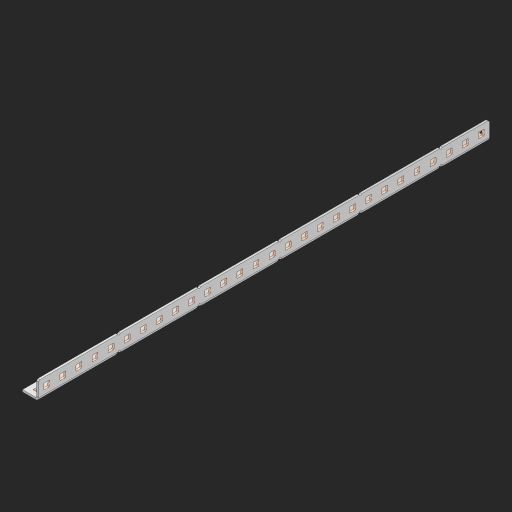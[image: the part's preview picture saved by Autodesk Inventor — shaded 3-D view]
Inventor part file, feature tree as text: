
AUTODESK INVENTOR PART (.ipt)
format: ipt  version: 2023 (Build 270158000, 158)  size: 921,088 bytes
history: native  units: in
note: dims shown in document units (in); Inventor stores cm internally (conversion verified against a paired STEP export)
features: other x61, extrude x55, sheet_metal_op x10, sketch x8, mirror x1, pattern_linear x1, chamfer x1
ambient origin geometry x8: Origin, YZ Plane, XZ Plane, XY Plane, X Axis, Y Axis, Z Axis, Center Point
bodies: Solid1 (feature_tree), Body (feature_tree)
feature tree (137):
  other  "Flange Pattern Plane"
  sheet_metal_op  "Flange Pattern"
  sheet_metal_op  "Body Pattern"
  other  "Arc Length"
  mirror  "Notch Mirror"
  pattern_linear  "Notch Pattern"  Spacing1=0.25in  [1 undecoded]
  chamfer  "End Chamfer"
  extrude  "Half Cut"  Depth=0.0625in
  sketch  "Sketch1"  dims[d0=1.5in]
  other  "Plate1"
  sketch  "Sketch2"  dims[d1=14.0in]
  other  "Plate2"
  sheet_metal_op  "Bend1"
  sheet_metal_op  "Corner1"
  sketch  "Sketch3"  dims[d2=0.0625in]
  other  "Flange Pattern Sketch"
  sketch  "Sketch7"  dims[d3=0.0625in]
  other  "Srf1"
  other  "Srf2"
  sketch  "Sketch8"  dims[d4=0.0312in]
  sketch  "Sketch9"  dims[d5=0.125in]
  other  "Srf91"
  sheet_metal_op  "Body Pattern Sketch"
  other  "Srf92"
  sketch  "Sketch13"  dims[d6=0.0625in]
  sketch  "Sketch14"  dims[d7=0.5in d8=90.0deg d9=0.0312in d10=0.25in d11=0.0625in d12=0.0625in d16=0.182in d17=0.02in d18=0.0625in d19=0.0in d20=0.25in d21=0.25in d46=0.172in d47=1.0in d48=0.0in d49=0.182in d50=0.02in d51=0.25in d52=0.25in d53=0.0625in d54=0.0in d55=0.172in d56=1.0in d57=0.0in d60=11.0236in d62=0.5in d63=0.3937in d65=0.5in d85=0.1473in d86=0.1782in d88=0.04in d89=0.0625in d90=0.0in d91=0.04in d92=0.0491in d95=2.5in d96=0.04in d97=0.25in d98=45.0deg d101=0.0in d102=2.497in d131=0.5in d132=11.0236in d134=0.5in d139=0.5in]
  other  "Srf856"
  other  "Srf1310"
  other  "Srf1311"
  other  "Srf1312"
  other  "Srf1376"
  other  "Srf1377"
  other  "Srf1728"
  other  "Srf1755"
  other  "Srf1878"
  other  "Srf1879"
  other  "Srf1880"
  other  "Srf1881"
  other  "Srf1882"
  other  "Srf1883"
  other  "Srf1884"
  other  "Srf1885"
  other  "Srf1886"
  other  "Srf1887"
  other  "Srf1888"
  other  "Srf1889"
  other  "Srf1890"
  other  "Srf1891"
  other  "Srf1892"
  other  "Srf1893"
  other  "Srf1894"
  other  "Srf1895"
  other  "Srf1896"
  other  "Srf1897"
  other  "Srf1898"
  other  "Srf1899"
  other  "Srf1942"
  other  "Srf1943"
  other  "Srf1944"
  other  "Srf1945"
  other  "Srf1946"
  other  "Srf1947"
  other  "Srf1948"
  other  "Srf1949"
  other  "Srf1950"
  other  "Srf1951"
  other  "Srf1952"
  other  "Srf1953"
  other  "Srf1954"
  other  "Srf1955"
  other  "Srf1956"
  other  "Srf1957"
  other  "Srf1958"
  other  "Srf1959"
  other  "Srf1960"
  other  "Srf1961"
  other  "Srf1962"
  other  "Srf1963"
  sheet_metal_op  "Flange Stamp"
  sheet_metal_op  "Flange Circle"
  sheet_metal_op  "Body Stamp"
  sheet_metal_op  "Body Circle"
  sheet_metal_op  "Notch"
  extrude  "ExtrusionSrf2"  Depth=0.0625in
  extrude  "ExtrusionSrf92"  Depth=0.5in
  extrude  "ExtrusionSrf856"  Depth=0.02in
  extrude  "ExtrusionSrf1310"  Depth=0.0625in
  extrude  "ExtrusionSrf1311"  TaperAngle=0.0deg  [1 undecoded]
  extrude  "ExtrusionSrf1312"  Depth=0.5in
  extrude  "ExtrusionSrf1376"  Depth=0.5in
  extrude  "ExtrusionSrf1377"  Depth=0.5in
  extrude  "ExtrusionSrf1728"  Depth=0.5in TaperAngle=0.0deg
  extrude  "ExtrusionSrf1755"  Depth=0.5in
  extrude  "ExtrusionSrf1878"  Depth=0.02in
  extrude  "ExtrusionSrf1879"  Depth=0.5in
  extrude  "ExtrusionSrf1880"  Depth=0.5in
  extrude  "ExtrusionSrf1881"  Depth=0.0625in
  extrude  "ExtrusionSrf1882"  TaperAngle=0.0deg  [1 undecoded]
  extrude  "ExtrusionSrf1883"  Depth=0.5in
  extrude  "ExtrusionSrf1884"  Depth=0.5in TaperAngle=0.0deg
  extrude  "ExtrusionSrf1885"  Depth=0.5in
  extrude  "ExtrusionSrf1886"  Depth=0.5in
  extrude  "ExtrusionSrf1887"  Depth=0.5in
  extrude  "ExtrusionSrf1888"  Depth=0.5in
  extrude  "ExtrusionSrf1889"  Depth=0.5in
  extrude  "ExtrusionSrf1890"  Depth=0.0625in
  extrude  "ExtrusionSrf1891"  TaperAngle=0.0deg  [1 undecoded]
  extrude  "ExtrusionSrf1892"  Depth=0.5in
  extrude  "ExtrusionSrf1893"  Depth=0.5in
  extrude  "ExtrusionSrf1894"  Depth=0.5in
  extrude  "ExtrusionSrf1895"  Depth=0.5in TaperAngle=45.0deg
  extrude  "ExtrusionSrf1896"  TaperAngle=0.0deg  [1 undecoded]
  extrude  "ExtrusionSrf1897"  Depth=0.5in
  extrude  "ExtrusionSrf1898"  Depth=0.5in
  extrude  "ExtrusionSrf1899"  Depth=0.5in
  extrude  "ExtrusionSrf1942"  Depth=0.5in
  extrude  "ExtrusionSrf1943"  Depth=0.5in
  extrude  "ExtrusionSrf1944"  [1 undecoded]
  extrude  "ExtrusionSrf1945"  [1 undecoded]
  extrude  "ExtrusionSrf1946"  [1 undecoded]
  extrude  "ExtrusionSrf1947"  [1 undecoded]
  extrude  "ExtrusionSrf1948"  [1 undecoded]
  extrude  "ExtrusionSrf1949"  [1 undecoded]
  extrude  "ExtrusionSrf1950"  [1 undecoded]
  extrude  "ExtrusionSrf1951"  [1 undecoded]
  extrude  "ExtrusionSrf1952"  [1 undecoded]
  extrude  "ExtrusionSrf1953"  [1 undecoded]
  extrude  "ExtrusionSrf1954"  [1 undecoded]
  extrude  "ExtrusionSrf1955"  [1 undecoded]
  extrude  "ExtrusionSrf1956"  [1 undecoded]
  extrude  "ExtrusionSrf1957"  [1 undecoded]
  extrude  "ExtrusionSrf1958"  [1 undecoded]
  extrude  "ExtrusionSrf1959"  [1 undecoded]
  extrude  "ExtrusionSrf1960"  [1 undecoded]
  extrude  "ExtrusionSrf1961"  [1 undecoded]
  extrude  "ExtrusionSrf1962"  [1 undecoded]
  extrude  "ExtrusionSrf1963"  [1 undecoded]
note: 25 required parameter values undecoded (feature->parameter linkage not recoverable at this tier; creation-order binding heuristic only, values carry confidence <= 0.55)
